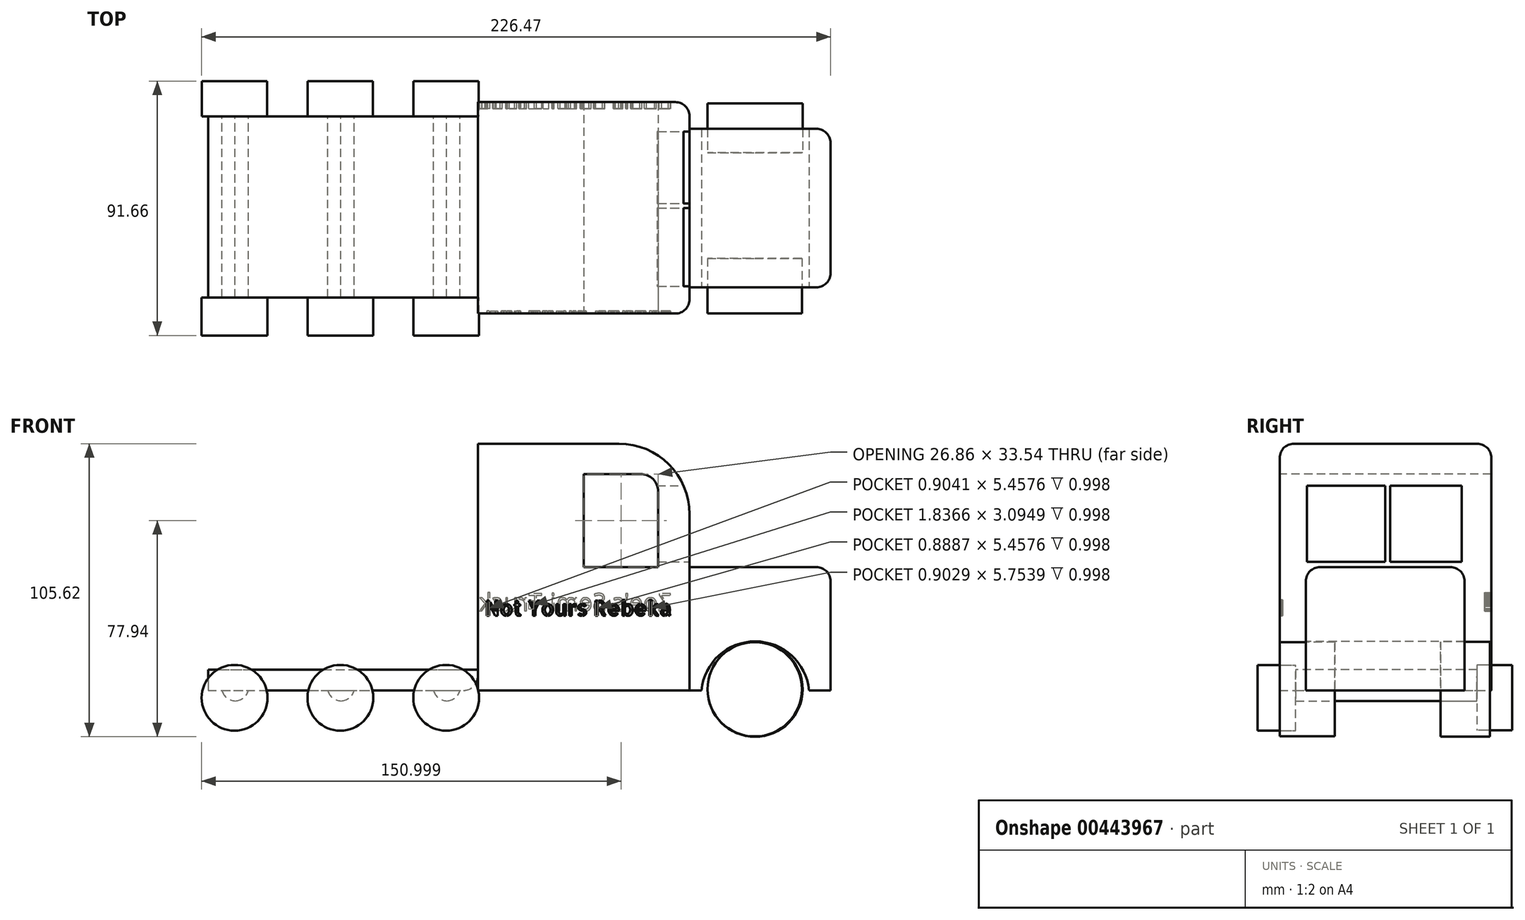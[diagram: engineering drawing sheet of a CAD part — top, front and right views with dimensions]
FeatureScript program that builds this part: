
annotation { "Feature Type Name" : "Feature", "Feature Type Description" : "" }
export const myFeature = defineFeature(function(context is Context, id is Id, definition is map)
    precondition{}
    {
        {
            var Q0;
            Q0=qCreatedBy(makeId("Front.planeOp"),FACE);
            var sketch = newSketch(context, id + "F0", { "sketchPlane" : qUnion([Q0])});
            skLineSegment(sketch, "E0.bottom", {"start": v(-38.1, 44.45) * mm, "end": v(38.1, 44.45) * mm});
            skLineSegment(sketch, "E0.top", {"start": v(-38.1, -44.45) * mm, "end": v(38.1, -44.45) * mm});
            skLineSegment(sketch, "E0.left", {"start": v(-38.1, 44.45) * mm, "end": v(-38.1, -44.45) * mm});
            skLineSegment(sketch, "E0.right", {"start": v(38.1, 44.45) * mm, "end": v(38.1, -44.45) * mm});
            skPoint(sketch, "E0.middle", {"position": v(0, 0) * mm});
            skSolve(sketch);
        }
        {
            var Q0;
            Q0=qSketchRegion(id+"F0",true);
            extrude(context, id + "F1", {"entities" : qUnion([Q0]), "depth" : 76.2 * mm});
        }
        {
            var Q0;
            Q0=makeQuery(id+"F1.opExtrude","SWEPT_EDGE",EDGE,{"disambiguationData":[OSD([sQuery(id+"F0.wireOp",EDGE,"E0.bottom"),sQuery(id+"F0.wireOp",EDGE,"E0.right")])]});
            fillet(context, id + "F2", {"entities" : qUnion([Q0]), "radius" : 25.4 * mm, "tangentPropagation" : true, "allowEdgeOverflow" : false});
        }
        {
            var Q0;
            {var subQ0=sQuery(id+"F0.wireOp",EDGE,"E0.right");var subQ1=sQuery(id+"F0.wireOp",EDGE,"E0.bottom");Q0=makeQuery(id+"F2.opFillet","BLEND_EDGE",EDGE,{"blendedFrom":[makeQuery(id+"F1.opExtrude","SWEPT_EDGE",EDGE,{"disambiguationData":[OSD([subQ1,subQ0])]}),makeQuery(id+"F1.opExtrude","CAP_FACE",FACE,{"disambiguationData":[OSD([subQ1,sQuery(id+"F0.wireOp",EDGE,"E0.top"),sQuery(id+"F0.wireOp",EDGE,"E0.left"),subQ0])],"isStart":true})],"blendedInto":[makeQuery(id+"F1.opExtrude","CAP_FACE",FACE,{"disambiguationData":[OSD([subQ1,sQuery(id+"F0.wireOp",EDGE,"E0.top"),sQuery(id+"F0.wireOp",EDGE,"E0.left"),subQ0])],"isStart":true})]});}
            fillet(context, id + "F3", {"entities" : qUnion([Q0]), "radius" : 5.08 * mm, "tangentPropagation" : true, "allowEdgeOverflow" : false});
        }
        {
            var Q0;
            Q0=makeQuery(id+"F1.opExtrude","CAP_EDGE",EDGE,{"disambiguationData":[OSD([sQuery(id+"F0.wireOp",EDGE,"E0.bottom")])],"isStart":false});
            fillet(context, id + "F4", {"entities" : qUnion([Q0]), "radius" : 5.08 * mm, "tangentPropagation" : true, "allowEdgeOverflow" : false});
        }
        {
            var Q0;
            Q0=makeQuery(id+"F1.opExtrude","SWEPT_FACE",FACE,{"disambiguationData":[OSD([sQuery(id+"F0.wireOp",EDGE,"E0.right")])]});
            var sketch = newSketch(context, id + "F5", { "sketchPlane" : qUnion([Q0])});
            skLineSegment(sketch, "E1.bottom", {"start": v(-66.78, 0) * mm, "end": v(-9.63, 0) * mm});
            skLineSegment(sketch, "E1.top", {"start": v(-66.78, -44.45) * mm, "end": v(-9.63, -44.45) * mm});
            skLineSegment(sketch, "E1.left", {"start": v(-66.78, 0) * mm, "end": v(-66.78, -44.45) * mm});
            skLineSegment(sketch, "E1.right", {"start": v(-9.63, 0) * mm, "end": v(-9.63, -44.45) * mm});
            skSolve(sketch);
        }
        {
            var Q0;
            Q0=makeQuery(id+"F5.imprint","IMPRINT",FACE,{"disambiguationData":[TD([[makeQuery(id+"F5.imprint","IMPRINT",EDGE,{"derivedFrom":sQuery(id+"F5.wireOp",EDGE,"E1.bottom")}),-1.0]])]});
            extrude(context, id + "F6", {"entities" : qUnion([Q0]), "operationType" : NewBodyOperationType.ADD, "depth" : 50.8 * mm});
        }
        {
            var Q0;
            Q0=makeQuery(id+"F6.opExtrude","CAP_EDGE",EDGE,{"disambiguationData":[OSD([sQuery(id+"F5.wireOp",EDGE,"E1.bottom")])],"isStart":false});
            var Q1;
            Q1=makeQuery(id+"F6.opExtrude","SWEPT_EDGE",EDGE,{"disambiguationData":[OSD([sQuery(id+"F5.wireOp",EDGE,"E1.bottom"),sQuery(id+"F5.wireOp",EDGE,"E1.right")])]});
            var Q2;
            Q2=makeQuery(id+"F6.opExtrude","SWEPT_EDGE",EDGE,{"disambiguationData":[OSD([sQuery(id+"F5.wireOp",EDGE,"E1.bottom"),sQuery(id+"F5.wireOp",EDGE,"E1.left")])]});
            var Q3;
            Q3=makeQuery(id+"F6.opExtrude","CAP_EDGE",EDGE,{"disambiguationData":[OSD([sQuery(id+"F5.wireOp",EDGE,"E1.left")])],"isStart":false});
            var Q4;
            Q4=makeQuery(id+"F6.opExtrude","CAP_EDGE",EDGE,{"disambiguationData":[OSD([sQuery(id+"F5.wireOp",EDGE,"E1.right")])],"isStart":false});
            fillet(context, id + "F7", {"entities" : qUnion([Q0, Q1, Q2, Q3, Q4]), "radius" : 5.08 * mm, "tangentPropagation" : true, "allowEdgeOverflow" : false});
        }
        {
            var Q0;
            Q0=makeQuery(id+"F6.opExtrude","SWEPT_FACE",FACE,{"disambiguationData":[OSD([sQuery(id+"F5.wireOp",EDGE,"E1.left")])]});
            var sketch = newSketch(context, id + "F8", { "sketchPlane" : qUnion([Q0])});
            skCircle(sketch, "E2", {"center": v(61.81, -46.27) * mm, "radius": 19.46 * mm});
            skSolve(sketch);
        }
        {
            var Q0;
            {var subQ0=sQuery(id+"F8.wireOp",EDGE,"E2");var subQ1=makeQuery(id+"F6.opExtrude","SWEPT_EDGE",EDGE,{"disambiguationData":[OSD([sQuery(id+"F0.wireOp",EDGE,"E0.top"),sQuery(id+"F0.wireOp",EDGE,"E0.right"),sQuery(id+"F5.wireOp",EDGE,"E1.top"),sQuery(id+"F5.wireOp",EDGE,"E1.left")])]});var subQ2=makeQuery(id+"F8.imprint","INTERSECT",VERTEX,{"disambiguationData":[OD(0.0)],"derivedFrom":[subQ1,subQ0]});Q0=makeQuery(id+"F8.imprint","IMPRINT",FACE,{"disambiguationData":[TD([[makeQuery(id+"F8.imprint","IMPRINT",EDGE,{"disambiguationData":[TD([[subQ2,1.0]])],"derivedFrom":subQ0}),1.0]])]});}
            extrude(context, id + "F9", {"entities" : qUnion([Q0]), "operationType" : NewBodyOperationType.REMOVE, "oppositeDirection" : true, "depth" : 198.74 * mm});
        }
        {
            var Q0;
            Q0=makeQuery(id+"F1.opExtrude","CAP_FACE",FACE,{"disambiguationData":[OSD([sQuery(id+"F0.wireOp",EDGE,"E0.bottom"),sQuery(id+"F0.wireOp",EDGE,"E0.top"),sQuery(id+"F0.wireOp",EDGE,"E0.left"),sQuery(id+"F0.wireOp",EDGE,"E0.right")])],"isStart":false});
            var sketch = newSketch(context, id + "F10", { "sketchPlane" : qUnion([Q0])});
            skLineSegment(sketch, "E3.bottom", {"start": v(0, 33.54) * mm, "end": v(20.5, 33.54) * mm});
            skLineSegment(sketch, "E3.top", {"start": v(0, 0) * mm, "end": v(26.86, 0) * mm});
            skLineSegment(sketch, "E3.left", {"start": v(0, 33.54) * mm, "end": v(0, 0) * mm});
            skLineSegment(sketch, "E3.right", {"start": v(26.86, 27.19) * mm, "end": v(26.86, 0) * mm});
            skPoint(sketch, "E4.visualSharp", {"position": v(26.86, 33.54) * mm});
            skArc(sketch, "E4.filletArc", {"start": v(26.86, 27.19) * mm, "mid": v(25, 31.68) * mm, "end": v(20.5, 33.54) * mm});
            skSolve(sketch);
        }
        {
            var Q0;
            Q0=makeQuery(id+"F10.imprint","IMPRINT",FACE,{"disambiguationData":[TD([[makeQuery(id+"F10.imprint","IMPRINT",EDGE,{"derivedFrom":sQuery(id+"F10.wireOp",EDGE,"E3.bottom")}),-1.0]])]});
            extrude(context, id + "F11", {"entities" : qUnion([Q0]), "operationType" : NewBodyOperationType.REMOVE, "oppositeDirection" : true, "depth" : 169.3 * mm});
        }
        {
            var Q0;
            Q0=makeQuery(id+"F1.opExtrude","SWEPT_FACE",FACE,{"disambiguationData":[OSD([sQuery(id+"F0.wireOp",EDGE,"E0.right")])]});
            var sketch = newSketch(context, id + "F12", { "sketchPlane" : qUnion([Q0])});
            skPoint(sketch, "E5.oppositeSnap0", {"position": v(-38.2, 0) * mm});
            skLineSegment(sketch, "E5.bottom", {"start": v(-66.37, 29.3) * mm, "end": v(-38.2, 29.3) * mm});
            skLineSegment(sketch, "E5.top", {"start": v(-66.37, 1.82) * mm, "end": v(-38.2, 1.82) * mm});
            skLineSegment(sketch, "E5.left", {"start": v(-66.37, 29.3) * mm, "end": v(-66.37, 1.82) * mm});
            skLineSegment(sketch, "E5.right", {"start": v(-38.2, 29.3) * mm, "end": v(-38.2, 1.82) * mm});
            skLineSegment(sketch, "E6.bottom", {"start": v(-36.47, 29.3) * mm, "end": v(-10.6, 29.3) * mm});
            skLineSegment(sketch, "E6.top", {"start": v(-36.47, 1.82) * mm, "end": v(-10.6, 1.82) * mm});
            skLineSegment(sketch, "E6.left", {"start": v(-36.47, 29.3) * mm, "end": v(-36.47, 1.82) * mm});
            skLineSegment(sketch, "E6.right", {"start": v(-10.6, 29.3) * mm, "end": v(-10.6, 1.82) * mm});
            skSolve(sketch);
        }
        {
            var Q0;
            Q0=qSketchRegion(id+"F12",true);
            extrude(context, id + "F13", {"entities" : qUnion([Q0]), "operationType" : NewBodyOperationType.REMOVE, "oppositeDirection" : true, "depth" : 25.4 * mm});
        }
        {
            var Q0;
            Q0=makeQuery(id+"F1.opExtrude","CAP_FACE",FACE,{"disambiguationData":[OSD([sQuery(id+"F0.wireOp",EDGE,"E0.bottom"),sQuery(id+"F0.wireOp",EDGE,"E0.top"),sQuery(id+"F0.wireOp",EDGE,"E0.left"),sQuery(id+"F0.wireOp",EDGE,"E0.right")])],"isStart":true});
            var sketch = newSketch(context, id + "F14", { "sketchPlane" : qUnion([Q0])});
            skText(sketch, "E7", { "text": "Zoe\'s Semi-Truck", "fontName": "OpenSans-Regular.ttf"});
            const initialGuessF14  = {"E7": [-0.03177, -0.01583, 1, 0, 0.00634]};
            skSetInitialGuess(sketch, initialGuessF14);
            skSolve(sketch);
        }
        {
            var Q0;
            Q0=qSketchRegion(id+"F14",true);
            extrude(context, id + "F15", {"entities" : qUnion([Q0]), "operationType" : NewBodyOperationType.REMOVE, "oppositeDirection" : true, "depth" : 2.36 * mm});
        }
        {
            var Q0;
            Q0=makeQuery(id+"F1.opExtrude","CAP_FACE",FACE,{"disambiguationData":[OSD([sQuery(id+"F0.wireOp",EDGE,"E0.bottom"),sQuery(id+"F0.wireOp",EDGE,"E0.top"),sQuery(id+"F0.wireOp",EDGE,"E0.left"),sQuery(id+"F0.wireOp",EDGE,"E0.right")])],"isStart":false});
            var sketch = newSketch(context, id + "F16", { "sketchPlane" : qUnion([Q0])});
            skText(sketch, "E8", { "text": "Not Yours Rebeka", "fontName": "AllertaStencil-Regular.ttf"});
            skPoint(sketch, "E9", {"position": v(33.02, -12.7) * mm});
            const initialGuessF16  = {"E8": [-0.03557, -0.01755, 1, 0, 0.00546]};
            skSetInitialGuess(sketch, initialGuessF16);
            skSolve(sketch);
        }
        {
            var Q0;
            Q0=qSketchRegion(id+"F16",true);
            extrude(context, id + "F17", {"entities" : qUnion([Q0]), "operationType" : NewBodyOperationType.REMOVE, "oppositeDirection" : true, "depth" : 1 * mm});
        }
        {
            var Q0;
            Q0=makeQuery(id+"F1.opExtrude","CAP_FACE",FACE,{"disambiguationData":[OSD([sQuery(id+"F0.wireOp",EDGE,"E0.bottom"),sQuery(id+"F0.wireOp",EDGE,"E0.top"),sQuery(id+"F0.wireOp",EDGE,"E0.left"),sQuery(id+"F0.wireOp",EDGE,"E0.right")])],"isStart":false});
            var sketch = newSketch(context, id + "F18", { "sketchPlane" : qUnion([Q0])});
            skCircle(sketch, "E10", {"center": v(61.6, -44.05) * mm, "radius": 16.98 * mm});
            skSolve(sketch);
        }
        {
            var Q0;
            Q0=makeQuery(id+"F18.imprint","IMPRINT",FACE,{"disambiguationData":[TD([[makeQuery(id+"F18.imprint","IMPRINT",EDGE,{"derivedFrom":sQuery(id+"F18.wireOp",EDGE,"E10")}),1.0]])]});
            extrude(context, id + "F19", {"entities" : qUnion([Q0]), "oppositeDirection" : true, "depth" : 19.87 * mm});
        }
        {
            var Q0;
            Q0=makeQuery(id+"F6.opExtrude","SWEPT_FACE",FACE,{"disambiguationData":[OSD([sQuery(id+"F5.wireOp",EDGE,"E1.right")])]});
            var sketch = newSketch(context, id + "F20", { "sketchPlane" : qUnion([Q0])});
            skCircle(sketch, "E11", {"center": v(-61.73, -44.04) * mm, "radius": 17.13 * mm});
            skPoint(sketch, "E11.first.point", {"position": v(-78.38, -40) * mm});
            skPoint(sketch, "E11.second.point", {"position": v(-45.04, -47.88) * mm});
            skPoint(sketch, "E11.third.point", {"position": v(-64.03, -61.02) * mm});
            skSolve(sketch);
        }
        {
            var Q0;
            Q0=makeQuery(id+"F20.imprint","IMPRINT",FACE,{"disambiguationData":[TD([[makeQuery(id+"F20.imprint","IMPRINT",EDGE,{"derivedFrom":sQuery(id+"F20.wireOp",EDGE,"E11")}),1.0]])]});
            extrude(context, id + "F21", {"entities" : qUnion([Q0]), "depth" : 9.14 * mm});
        }
        {
            var Q0;
            Q0=qSketchRegion(id+"F20",true);
            extrude(context, id + "F22", {"entities" : qUnion([Q0]), "operationType" : NewBodyOperationType.ADD, "oppositeDirection" : true, "depth" : 8.57 * mm});
        }
        {
            var Q0;
            Q0=makeQuery(id+"F1.opExtrude","SWEPT_FACE",FACE,{"disambiguationData":[OSD([sQuery(id+"F0.wireOp",EDGE,"E0.left")])]});
            var sketch = newSketch(context, id + "F23", { "sketchPlane" : qUnion([Q0])});
            skLineSegment(sketch, "E12.bottom", {"start": v(5.15, -36.97) * mm, "end": v(70.41, -36.97) * mm});
            skLineSegment(sketch, "E12.top", {"start": v(5.15, -44.45) * mm, "end": v(70.41, -44.45) * mm});
            skLineSegment(sketch, "E12.left", {"start": v(5.15, -36.97) * mm, "end": v(5.15, -44.45) * mm});
            skLineSegment(sketch, "E12.right", {"start": v(70.41, -36.97) * mm, "end": v(70.41, -44.45) * mm});
            skSolve(sketch);
        }
        {
            var Q0;
            Q0=qSketchRegion(id+"F23",true);
            extrude(context, id + "F24", {"entities" : qUnion([Q0]), "depth" : 97.15 * mm});
        }
        {
            var Q0;
            Q0=makeQuery(id+"F24.opExtrude","SWEPT_FACE",FACE,{"disambiguationData":[OSD([sQuery(id+"F23.wireOp",EDGE,"E12.left")])]});
            var sketch = newSketch(context, id + "F25", { "sketchPlane" : qUnion([Q0])});
            skCircle(sketch, "E13", {"center": v(49.54, -47.08) * mm, "radius": 11.75 * mm});
            skCircle(sketch, "E14.1.0.0", {"center": v(87.64, -47.08) * mm, "radius": 11.75 * mm});
            skCircle(sketch, "E14.2.0.0", {"center": v(125.74, -47.08) * mm, "radius": 11.75 * mm});
            skLineSegment(sketch, "E14.direction1", {"start": v(49.54, -47.08) * mm, "end": v(87.64, -47.08) * mm, "construction": true});
            skSolve(sketch);
        }
        {
            var Q0;
            Q0=qSketchRegion(id+"F25",true);
            extrude(context, id + "F26", {"entities" : qUnion([Q0]), "depth" : 12.7 * mm});
        }
        {
            var Q0;
            Q0=makeQuery(id+"F24.opExtrude","SWEPT_FACE",FACE,{"disambiguationData":[OSD([sQuery(id+"F23.wireOp",EDGE,"E12.top")])]});
            var sketch = newSketch(context, id + "F27", { "sketchPlane" : qUnion([Q0])});
            skLineSegment(sketch, "E15.bottom", {"start": v(-130.27, 70.41) * mm, "end": v(-120.77, 70.41) * mm});
            skLineSegment(sketch, "E15.top", {"start": v(-130.27, 5.15) * mm, "end": v(-120.77, 5.15) * mm});
            skLineSegment(sketch, "E15.left", {"start": v(-130.27, 70.41) * mm, "end": v(-130.27, 5.15) * mm});
            skLineSegment(sketch, "E15.right", {"start": v(-120.77, 70.41) * mm, "end": v(-120.77, 5.15) * mm});
            skLineSegment(sketch, "E16.1.0.0", {"start": v(-92.17, 70.41) * mm, "end": v(-92.17, 5.15) * mm});
            skLineSegment(sketch, "E16.1.0.1", {"start": v(-82.67, 70.41) * mm, "end": v(-82.67, 5.15) * mm});
            skLineSegment(sketch, "E16.1.0.2", {"start": v(-92.17, 70.41) * mm, "end": v(-82.67, 70.41) * mm});
            skLineSegment(sketch, "E16.1.0.3", {"start": v(-92.17, 5.15) * mm, "end": v(-82.67, 5.15) * mm});
            skLineSegment(sketch, "E16.2.0.0", {"start": v(-54.07, 70.41) * mm, "end": v(-54.07, 5.15) * mm});
            skLineSegment(sketch, "E16.2.0.1", {"start": v(-44.57, 70.41) * mm, "end": v(-44.57, 5.15) * mm});
            skLineSegment(sketch, "E16.2.0.2", {"start": v(-54.07, 70.41) * mm, "end": v(-44.57, 70.41) * mm});
            skLineSegment(sketch, "E16.2.0.3", {"start": v(-54.07, 5.15) * mm, "end": v(-44.57, 5.15) * mm});
            skLineSegment(sketch, "E16.direction1", {"start": v(-130.27, 5.15) * mm, "end": v(-92.17, 5.15) * mm, "construction": true});
            skSolve(sketch);
        }
        {
            var Q0;
            Q0=qSketchRegion(id+"F27",true);
            extrude(context, id + "F28", {"entities" : qUnion([Q0]), "depth" : 3.8 * mm});
        }
        {
            var Q0;
            Q0=makeQuery(id+"F28.opExtrude","CAP_EDGE",EDGE,{"disambiguationData":[OSD([sQuery(id+"F27.wireOp",EDGE,"E15.left")])],"isStart":false});
            var Q1;
            Q1=makeQuery(id+"F28.opExtrude","CAP_EDGE",EDGE,{"disambiguationData":[OSD([sQuery(id+"F27.wireOp",EDGE,"E15.right")])],"isStart":false});
            var Q2;
            Q2=makeQuery(id+"F28.opExtrude","CAP_EDGE",EDGE,{"disambiguationData":[OSD([sQuery(id+"F27.wireOp",EDGE,"E16.1.0.0")])],"isStart":false});
            var Q3;
            Q3=makeQuery(id+"F28.opExtrude","CAP_EDGE",EDGE,{"disambiguationData":[OSD([sQuery(id+"F27.wireOp",EDGE,"E16.1.0.1")])],"isStart":false});
            var Q4;
            Q4=makeQuery(id+"F28.opExtrude","CAP_EDGE",EDGE,{"disambiguationData":[OSD([sQuery(id+"F27.wireOp",EDGE,"E16.2.0.0")])],"isStart":false});
            var Q5;
            Q5=makeQuery(id+"F24.opExtrude","CAP_EDGE",EDGE,{"disambiguationData":[OSD([sQuery(id+"F23.wireOp",EDGE,"E12.top")])],"isStart":true});
            fillet(context, id + "F29", {"entities" : qUnion([Q0, Q1, Q2, Q3, Q4, Q5]), "radius" : 5.08 * mm, "tangentPropagation" : true, "allowEdgeOverflow" : false});
        }
        {
            var Q0;
            Q0=makeQuery(id+"F28.opExtrude","CAP_EDGE",EDGE,{"disambiguationData":[OSD([sQuery(id+"F27.wireOp",EDGE,"E16.2.0.1")])],"isStart":false});
            fillet(context, id + "F30", {"entities" : qUnion([Q0]), "radius" : 5.08 * mm, "tangentPropagation" : true, "allowEdgeOverflow" : false});
        }
        {
            var Q0;
            Q0=makeQuery(id+"F24.opExtrude","SWEPT_FACE",FACE,{"disambiguationData":[OSD([sQuery(id+"F23.wireOp",EDGE,"E12.right")])]});
            var sketch = newSketch(context, id + "F31", { "sketchPlane" : qUnion([Q0])});
            skCircle(sketch, "E17", {"center": v(-125.73, -47.13) * mm, "radius": 11.84 * mm});
            skPoint(sketch, "E17.first.point", {"position": v(-137.54, -46.27) * mm});
            skPoint(sketch, "E17.second.point", {"position": v(-113.9, -47.68) * mm});
            skPoint(sketch, "E17.third.point", {"position": v(-120.57, -57.79) * mm});
            skCircle(sketch, "E18.1.0.0", {"center": v(-87.63, -47.13) * mm, "radius": 11.84 * mm});
            skCircle(sketch, "E18.2.0.0", {"center": v(-49.53, -47.13) * mm, "radius": 11.84 * mm});
            skLineSegment(sketch, "E18.direction1", {"start": v(-125.73, -47.13) * mm, "end": v(-87.63, -47.13) * mm, "construction": true});
            skSolve(sketch);
        }
        {
            var Q0;
            Q0=qSketchRegion(id+"F31",true);
            extrude(context, id + "F32", {"entities" : qUnion([Q0]), "depth" : 13.7 * mm});
        }
    });
